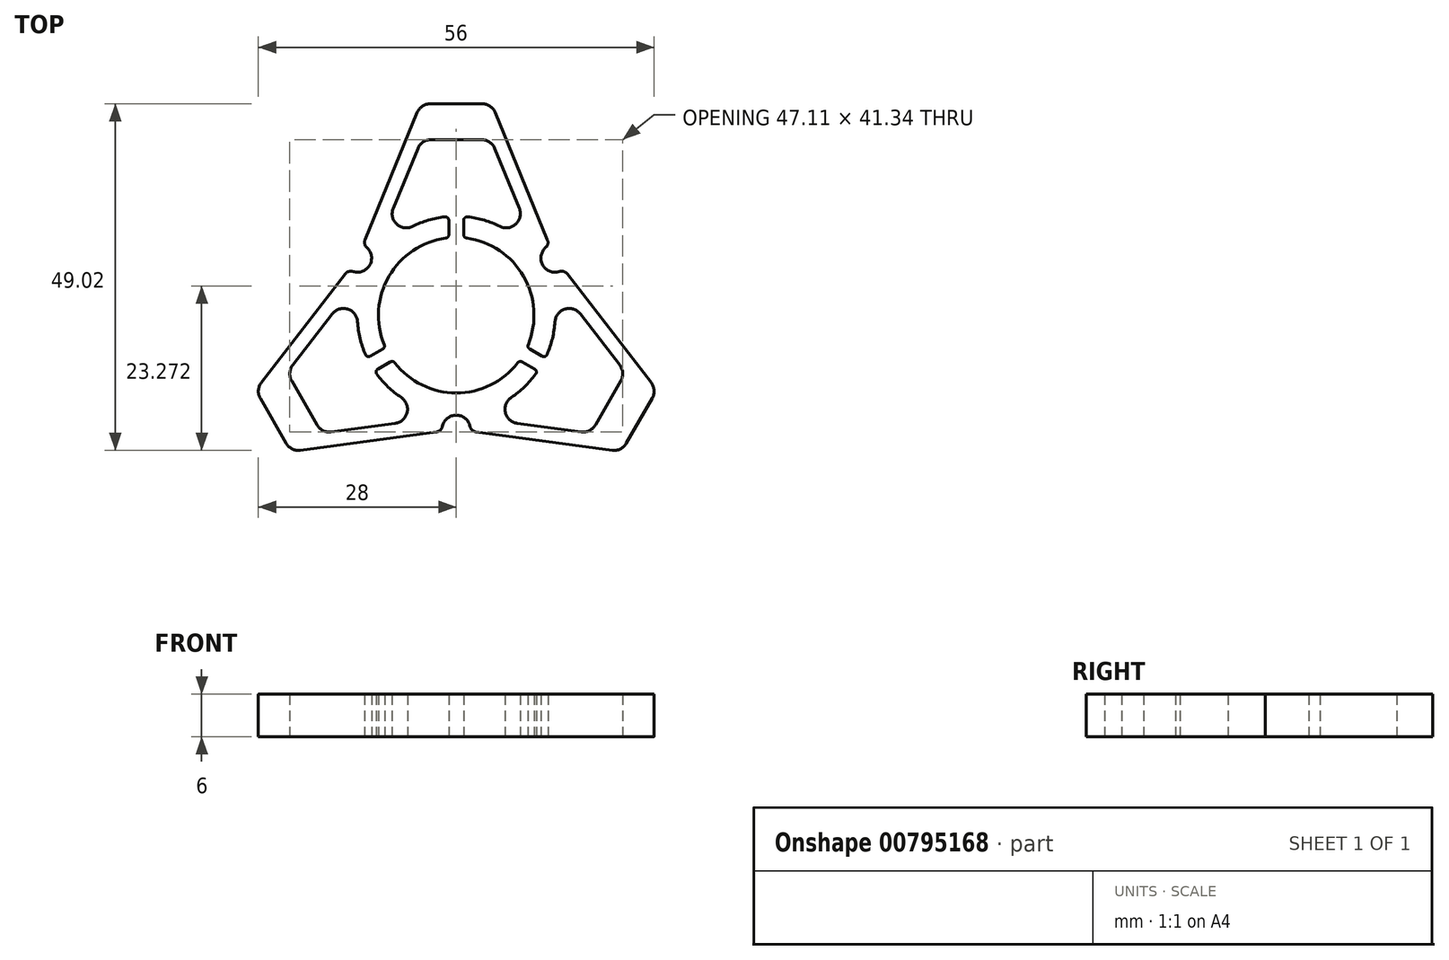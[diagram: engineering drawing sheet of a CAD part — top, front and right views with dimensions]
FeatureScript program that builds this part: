
annotation { "Feature Type Name" : "Feature", "Feature Type Description" : "" }
export const myFeature = defineFeature(function(context is Context, id is Id, definition is map)
    precondition{}
    {
        {
            var Q0;
            Q0=qCreatedBy(makeId("Top.planeOp"),FACE);
            var sketch = newSketch(context, id + "F0", { "sketchPlane" : qUnion([Q0])});
            skArc(sketch, "E0", {"start": v(-1.48, 10.9) * mm, "mid": v(-9.53, 5.5) * mm, "end": v(-10.18, -4.17) * mm});
            skArc(sketch, "E1", {"start": v(-1.6, 13.9) * mm, "mid": v(-3.96, 13.43) * mm, "end": v(-6.19, 12.56) * mm});
            skLineSegment(sketch, "E2.left", {"start": v(1.05, 11.4) * mm, "end": v(1.05, 13.41) * mm});
            skLineSegment(sketch, "E2.right", {"start": v(-1.05, 11.4) * mm, "end": v(-1.05, 13.41) * mm});
            skPoint(sketch, "E2.middle", {"position": v(0, 11) * mm});
            skPoint(sketch, "E2.bottom.end.orphan", {"position": v(-1.05, 5.48) * mm});
            skPoint(sketch, "E3.orphan", {"position": v(1.05, 5.6) * mm});
            skPoint(sketch, "E2.top.end.orphan", {"position": v(-1.05, 16.4) * mm});
            skPoint(sketch, "E2.top.start.orphan", {"position": v(1.05, 16.52) * mm});
            skPoint(sketch, "E4.visualSharp", {"position": v(-1.05, 10.95) * mm});
            skArc(sketch, "E4.filletArc", {"start": v(-1.48, 10.9) * mm, "mid": v(-1.17, 11.07) * mm, "end": v(-1.05, 11.4) * mm});
            skPoint(sketch, "E5.visualSharp", {"position": v(1.05, 10.95) * mm});
            skArc(sketch, "E5.filletArc", {"start": v(1.05, 11.4) * mm, "mid": v(1.17, 11.07) * mm, "end": v(1.48, 10.9) * mm});
            skPoint(sketch, "E6.visualSharp", {"position": v(-1.05, 13.96) * mm});
            skArc(sketch, "E6.filletArc", {"start": v(-1.05, 13.41) * mm, "mid": v(-1.22, 13.78) * mm, "end": v(-1.6, 13.9) * mm});
            skPoint(sketch, "E7.visualSharp", {"position": v(1.05, 13.96) * mm});
            skArc(sketch, "E7.filletArc", {"start": v(1.6, 13.9) * mm, "mid": v(1.22, 13.78) * mm, "end": v(1.05, 13.41) * mm});
            skLineSegment(sketch, "E8", {"start": v(0, 0) * mm, "end": v(0, 30.93) * mm, "construction": true});
            skLineSegment(sketch, "E9", {"start": v(-3.66, 29.9) * mm, "end": v(3.66, 29.9) * mm});
            skCircle(sketch, "E10", {"center": v(0, 0) * mm, "radius": 16 * mm, "construction": true});
            skLineSegment(sketch, "E11", {"start": v(5.5, 28.67) * mm, "end": v(12.9, 10.69) * mm});
            skLineSegment(sketch, "E12", {"start": v(-5.5, 28.67) * mm, "end": v(-12.9, 10.69) * mm});
            skPoint(sketch, "E13.visualSharp", {"position": v(5, 29.9) * mm});
            skArc(sketch, "E13.filletArc", {"start": v(5.5, 28.67) * mm, "mid": v(4.77, 29.57) * mm, "end": v(3.66, 29.9) * mm});
            skPoint(sketch, "E14.visualSharp", {"position": v(-5, 29.9) * mm});
            skArc(sketch, "E14.filletArc", {"start": v(-3.66, 29.9) * mm, "mid": v(-4.77, 29.57) * mm, "end": v(-5.5, 28.67) * mm});
            skLineSegment(sketch, "E15.0", {"start": v(5.44, 23.58) * mm, "end": v(8.92, 15.11) * mm});
            skLineSegment(sketch, "E15.2", {"start": v(-5.44, 23.58) * mm, "end": v(-8.92, 15.11) * mm});
            skPoint(sketch, "E16.visualSharp", {"position": v(14.04, 7.94) * mm});
            skLineSegment(sketch, "E17", {"start": v(-31.83, 0) * mm, "end": v(29.08, 0) * mm, "construction": true});
            skArc(sketch, "E18.trimOffspring", {"start": v(6.19, 12.56) * mm, "mid": v(3.96, 13.43) * mm, "end": v(1.6, 13.9) * mm});
            skArc(sketch, "E19.trimOffspring", {"start": v(-14, 0) * mm, "mid": v(-14, -0.46) * mm, "end": v(-13.97, -0.92) * mm});
            skPoint(sketch, "E20.visualSharp", {"position": v(-12.95, 5.33) * mm});
            skArc(sketch, "E20.filletArc", {"start": v(-8.92, 15.11) * mm, "mid": v(-8.44, 12.9) * mm, "end": v(-6.19, 12.56) * mm});
            skPoint(sketch, "E21.visualSharp", {"position": v(12.95, 5.33) * mm});
            skArc(sketch, "E21.filletArc", {"start": v(6.19, 12.56) * mm, "mid": v(8.44, 12.9) * mm, "end": v(8.92, 15.11) * mm});
            skLineSegment(sketch, "E22", {"start": v(-3.59, 24.82) * mm, "end": v(3.59, 24.82) * mm});
            skPoint(sketch, "E23.visualSharp", {"position": v(-4.93, 24.82) * mm});
            skArc(sketch, "E23.filletArc", {"start": v(-3.59, 24.82) * mm, "mid": v(-4.7, 24.48) * mm, "end": v(-5.44, 23.58) * mm});
            skPoint(sketch, "E24.visualSharp", {"position": v(4.93, 24.82) * mm});
            skArc(sketch, "E24.filletArc", {"start": v(5.44, 23.58) * mm, "mid": v(4.7, 24.48) * mm, "end": v(3.59, 24.82) * mm});
            skPoint(sketch, "E25.1.0", {"position": v(-8.96, -6.38) * mm});
            skArc(sketch, "E25.1.1", {"start": v(-13.97, -0.92) * mm, "mid": v(-15.38, 0.86) * mm, "end": v(-17.55, 0.17) * mm});
            skPoint(sketch, "E25.1.2", {"position": v(-5.37, -1.89) * mm});
            skPoint(sketch, "E25.1.3", {"position": v(-12.61, -6.07) * mm});
            skPoint(sketch, "E25.1.4", {"position": v(-13.9, 8.19) * mm});
            skArc(sketch, "E25.1.5", {"start": v(-8.63, -15.28) * mm, "mid": v(-6.95, -13.75) * mm, "end": v(-7.78, -11.64) * mm});
            skPoint(sketch, "E25.1.6", {"position": v(-4.22, -3.65) * mm});
            skLineSegment(sketch, "E25.1.7", {"start": v(-17.7, -16.5) * mm, "end": v(-8.63, -15.28) * mm});
            skPoint(sketch, "E25.1.8", {"position": v(-10, -4.57) * mm});
            skPoint(sketch, "E25.1.9", {"position": v(-23.96, -8.14) * mm});
            skLineSegment(sketch, "E25.1.10", {"start": v(-19.7, -15.52) * mm, "end": v(-23.3, -9.3) * mm});
            skLineSegment(sketch, "E25.1.11", {"start": v(-22.07, -19.1) * mm, "end": v(-2.8, -16.52) * mm});
            skLineSegment(sketch, "E25.1.12", {"start": v(-27.58, -9.56) * mm, "end": v(-15.7, 5.83) * mm});
            skLineSegment(sketch, "E25.1.13", {"start": v(-24.07, -18.12) * mm, "end": v(-27.73, -11.78) * mm});
            skPoint(sketch, "E25.1.14", {"position": v(-23.4, -19.28) * mm});
            skArc(sketch, "E25.1.15", {"start": v(-11.24, -8.35) * mm, "mid": v(-9.65, -10.14) * mm, "end": v(-7.78, -11.64) * mm});
            skPoint(sketch, "E25.1.16", {"position": v(-28.4, -10.62) * mm});
            skPoint(sketch, "E25.1.17", {"position": v(-14.83, -7.35) * mm});
            skPoint(sketch, "E25.1.18", {"position": v(-11.09, 8.55) * mm});
            skPoint(sketch, "E25.1.19", {"position": v(-19.03, -16.68) * mm});
            skPoint(sketch, "E25.1.20", {"position": v(-13.68, -9.11) * mm});
            skLineSegment(sketch, "E25.1.21", {"start": v(-23.14, -7.08) * mm, "end": v(-17.55, 0.17) * mm});
            skPoint(sketch, "E25.1.22", {"position": v(1.86, -13.88) * mm});
            skArc(sketch, "E25.1.23", {"start": v(-13.97, -0.92) * mm, "mid": v(-13.6, -3.29) * mm, "end": v(-12.85, -5.56) * mm});
            skPoint(sketch, "E25.1.24", {"position": v(-9.53, -5.5) * mm});
            skPoint(sketch, "E25.1.25", {"position": v(-11.57, -7.89) * mm});
            skArc(sketch, "E25.1.26", {"start": v(-19.7, -15.52) * mm, "mid": v(-18.85, -16.31) * mm, "end": v(-17.7, -16.5) * mm});
            skArc(sketch, "E25.1.27", {"start": v(-23.14, -7.08) * mm, "mid": v(-23.55, -8.17) * mm, "end": v(-23.3, -9.3) * mm});
            skArc(sketch, "E25.1.29", {"start": v(-24.07, -18.12) * mm, "mid": v(-23.22, -18.92) * mm, "end": v(-22.07, -19.1) * mm});
            skArc(sketch, "E25.1.30", {"start": v(-27.58, -9.56) * mm, "mid": v(-28, -10.65) * mm, "end": v(-27.73, -11.78) * mm});
            skArc(sketch, "E25.1.31", {"start": v(-11.09, -7.61) * mm, "mid": v(-11.33, -7.95) * mm, "end": v(-11.24, -8.35) * mm});
            skLineSegment(sketch, "E25.1.32", {"start": v(-9.34, -6.6) * mm, "end": v(-11.09, -7.61) * mm});
            skArc(sketch, "E25.1.33", {"start": v(-12.85, -5.56) * mm, "mid": v(-12.55, -5.84) * mm, "end": v(-12.14, -5.8) * mm});
            skArc(sketch, "E25.1.34", {"start": v(-10.4, -4.79) * mm, "mid": v(-10.17, -4.52) * mm, "end": v(-10.18, -4.17) * mm});
            skArc(sketch, "E25.1.35", {"start": v(-8.7, -6.73) * mm, "mid": v(-9, -6.55) * mm, "end": v(-9.34, -6.6) * mm});
            skLineSegment(sketch, "E25.1.36", {"start": v(-10.4, -4.79) * mm, "end": v(-12.14, -5.8) * mm});
            skPoint(sketch, "E25.2.0", {"position": v(10, -4.57) * mm});
            skArc(sketch, "E25.2.1", {"start": v(7.78, -11.64) * mm, "mid": v(6.95, -13.75) * mm, "end": v(8.63, -15.28) * mm});
            skPoint(sketch, "E25.2.2", {"position": v(4.32, -3.7) * mm});
            skPoint(sketch, "E25.2.3", {"position": v(11.57, -7.89) * mm});
            skPoint(sketch, "E25.2.4", {"position": v(-0.15, -16.12) * mm});
            skArc(sketch, "E25.2.5", {"start": v(17.55, 0.17) * mm, "mid": v(15.38, 0.86) * mm, "end": v(13.97, -0.92) * mm});
            skPoint(sketch, "E25.2.6", {"position": v(5.27, -1.83) * mm});
            skLineSegment(sketch, "E25.2.7", {"start": v(23.14, -7.08) * mm, "end": v(17.55, 0.17) * mm});
            skPoint(sketch, "E25.2.8", {"position": v(8.96, -6.38) * mm});
            skPoint(sketch, "E25.2.9", {"position": v(19.03, -16.68) * mm});
            skLineSegment(sketch, "E25.2.10", {"start": v(23.3, -9.3) * mm, "end": v(19.7, -15.52) * mm});
            skLineSegment(sketch, "E25.2.11", {"start": v(27.58, -9.56) * mm, "end": v(15.7, 5.83) * mm});
            skLineSegment(sketch, "E25.2.12", {"start": v(22.07, -19.1) * mm, "end": v(2.8, -16.52) * mm});
            skLineSegment(sketch, "E25.2.13", {"start": v(27.73, -11.78) * mm, "end": v(24.07, -18.12) * mm});
            skPoint(sketch, "E25.2.14", {"position": v(28.4, -10.62) * mm});
            skArc(sketch, "E25.2.15", {"start": v(12.85, -5.56) * mm, "mid": v(13.6, -3.29) * mm, "end": v(13.97, -0.92) * mm});
            skPoint(sketch, "E25.2.16", {"position": v(23.4, -19.28) * mm});
            skPoint(sketch, "E25.2.17", {"position": v(13.78, -9.17) * mm});
            skPoint(sketch, "E25.2.18", {"position": v(-1.86, -13.88) * mm});
            skPoint(sketch, "E25.2.19", {"position": v(23.96, -8.14) * mm});
            skPoint(sketch, "E25.2.20", {"position": v(14.73, -7.3) * mm});
            skLineSegment(sketch, "E25.2.21", {"start": v(17.7, -16.5) * mm, "end": v(8.63, -15.28) * mm});
            skPoint(sketch, "E25.2.22", {"position": v(11.09, 8.55) * mm});
            skArc(sketch, "E25.2.23", {"start": v(7.78, -11.64) * mm, "mid": v(9.65, -10.14) * mm, "end": v(11.24, -8.35) * mm});
            skPoint(sketch, "E25.2.24", {"position": v(9.53, -5.5) * mm});
            skPoint(sketch, "E25.2.25", {"position": v(12.61, -6.07) * mm});
            skArc(sketch, "E25.2.26", {"start": v(23.3, -9.3) * mm, "mid": v(23.55, -8.17) * mm, "end": v(23.14, -7.08) * mm});
            skArc(sketch, "E25.2.27", {"start": v(17.7, -16.5) * mm, "mid": v(18.85, -16.31) * mm, "end": v(19.7, -15.52) * mm});
            skArc(sketch, "E25.2.29", {"start": v(27.73, -11.78) * mm, "mid": v(28, -10.65) * mm, "end": v(27.58, -9.56) * mm});
            skArc(sketch, "E25.2.30", {"start": v(22.07, -19.1) * mm, "mid": v(23.22, -18.92) * mm, "end": v(24.07, -18.12) * mm});
            skArc(sketch, "E25.2.31", {"start": v(12.14, -5.8) * mm, "mid": v(12.55, -5.84) * mm, "end": v(12.85, -5.56) * mm});
            skLineSegment(sketch, "E25.2.32", {"start": v(10.4, -4.79) * mm, "end": v(12.14, -5.8) * mm});
            skArc(sketch, "E25.2.33", {"start": v(11.24, -8.35) * mm, "mid": v(11.33, -7.95) * mm, "end": v(11.09, -7.61) * mm});
            skArc(sketch, "E25.2.34", {"start": v(9.34, -6.6) * mm, "mid": v(9, -6.55) * mm, "end": v(8.7, -6.73) * mm});
            skArc(sketch, "E25.2.35", {"start": v(10.18, -4.17) * mm, "mid": v(10.17, -4.52) * mm, "end": v(10.4, -4.79) * mm});
            skLineSegment(sketch, "E25.2.36", {"start": v(9.34, -6.6) * mm, "end": v(11.09, -7.61) * mm});
            skPoint(sketch, "E26.orphan", {"position": v(-14.8, 6.09) * mm});
            skPoint(sketch, "E27.orphan", {"position": v(-12.67, 9.77) * mm});
            skPoint(sketch, "E28.orphan", {"position": v(14.8, 6.09) * mm});
            skArc(sketch, "E29.trimOffspring", {"start": v(10.18, -4.17) * mm, "mid": v(9.53, 5.5) * mm, "end": v(1.48, 10.9) * mm});
            skArc(sketch, "E30.trimOffspring", {"start": v(-8.7, -6.73) * mm, "mid": v(0, -11) * mm, "end": v(8.7, -6.73) * mm});
            skArc(sketch, "E31", {"start": v(12.65, 9.56) * mm, "mid": v(12.25, 7.07) * mm, "end": v(14.6, 6.17) * mm});
            skArc(sketch, "E32", {"start": v(-14.6, 6.17) * mm, "mid": v(-12.25, 7.07) * mm, "end": v(-12.65, 9.56) * mm});
            skArc(sketch, "E33", {"start": v(1.96, -15.73) * mm, "mid": v(0, -14.14) * mm, "end": v(-1.96, -15.73) * mm});
            skPoint(sketch, "E34.visualSharp", {"position": v(13.22, 9.92) * mm});
            skArc(sketch, "E34.filletArc", {"start": v(12.65, 9.56) * mm, "mid": v(12.95, 10.08) * mm, "end": v(12.9, 10.69) * mm});
            skPoint(sketch, "E35.visualSharp", {"position": v(15.2, 6.49) * mm});
            skArc(sketch, "E35.filletArc", {"start": v(15.7, 5.83) * mm, "mid": v(15.2, 6.18) * mm, "end": v(14.6, 6.17) * mm});
            skPoint(sketch, "E36.visualSharp", {"position": v(1.98, -16.4) * mm});
            skArc(sketch, "E36.filletArc", {"start": v(1.96, -15.73) * mm, "mid": v(2.26, -16.26) * mm, "end": v(2.8, -16.52) * mm});
            skPoint(sketch, "E37.visualSharp", {"position": v(-1.98, -16.4) * mm});
            skArc(sketch, "E37.filletArc", {"start": v(-2.8, -16.52) * mm, "mid": v(-2.26, -16.26) * mm, "end": v(-1.96, -15.73) * mm});
            skPoint(sketch, "E38.visualSharp", {"position": v(-15.2, 6.49) * mm});
            skArc(sketch, "E38.filletArc", {"start": v(-14.6, 6.17) * mm, "mid": v(-15.2, 6.18) * mm, "end": v(-15.7, 5.83) * mm});
            skPoint(sketch, "E39.visualSharp", {"position": v(-13.22, 9.92) * mm});
            skArc(sketch, "E39.filletArc", {"start": v(-12.9, 10.69) * mm, "mid": v(-12.95, 10.08) * mm, "end": v(-12.65, 9.56) * mm});
            skSolve(sketch);
        }
        {
            var Q0;
            Q0 = qSketchRegion(id + "F0", true);
            extrude(context, id + "F1", {"entities" : qUnion([Q0]), "depth" : 6 * mm, "offsetDistance" : 25 * mm});
        }
    });
